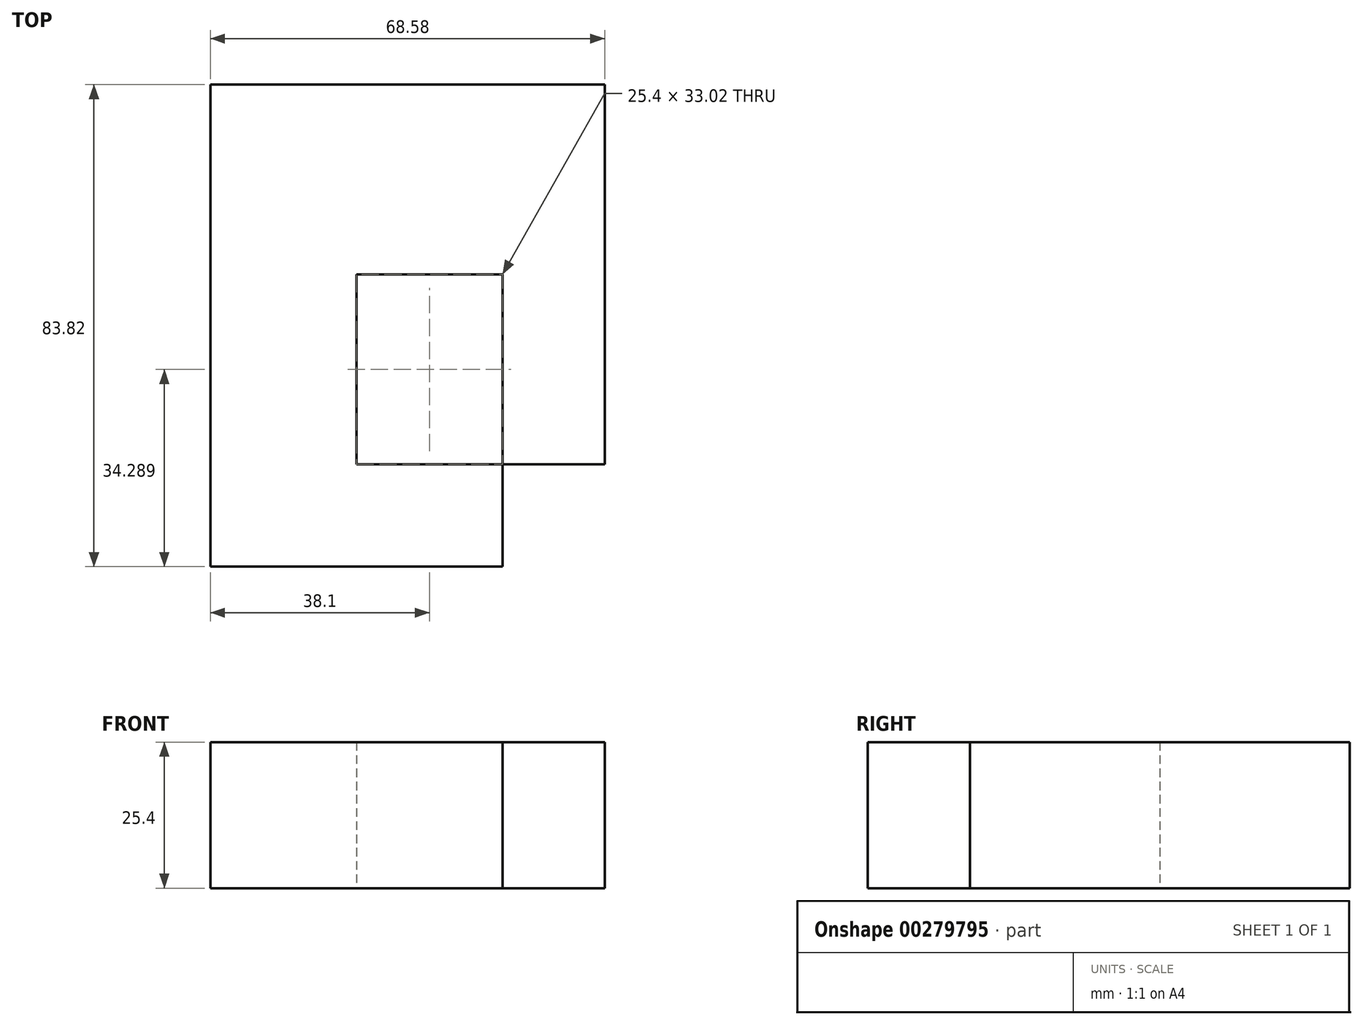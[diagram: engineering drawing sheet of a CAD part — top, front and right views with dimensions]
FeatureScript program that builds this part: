
annotation { "Feature Type Name" : "Feature", "Feature Type Description" : "" }
export const myFeature = defineFeature(function(context is Context, id is Id, definition is map)
    precondition{}
    {
        {
            var Q0;
            Q0=qCreatedBy(makeId("Right.planeOp"),FACE);
            var sketch = newSketch(context, id + "F0", { "sketchPlane" : qUnion([Q0])});
            skLineSegment(sketch, "E0.bottom", {"start": v(-62.3, -39.55) * mm, "end": v(3.74, -39.55) * mm});
            skLineSegment(sketch, "E0.top", {"start": v(-62.3, -64.95) * mm, "end": v(3.74, -64.95) * mm});
            skLineSegment(sketch, "E0.left", {"start": v(-62.3, -39.55) * mm, "end": v(-62.3, -64.95) * mm});
            skLineSegment(sketch, "E0.right", {"start": v(3.74, -39.55) * mm, "end": v(3.74, -64.95) * mm});
            skLineSegment(sketch, "E1", {"start": v(-29.28, -39.55) * mm, "end": v(-29.28, -64.95) * mm});
            skSolve(sketch);
        }
        {
            var Q0;
            {var subQ0=sQuery(id+"F0.wireOp",EDGE,"E0.left");Q0=makeQuery(id+"F0.imprint","IMPRINT",FACE,{"disambiguationData":[TD([[makeQuery(id+"F0.imprint","IMPRINT",EDGE,{"derivedFrom":subQ0}),1.0]])]});}
            extrude(context, id + "F1", {"entities" : qUnion([Q0]), "oppositeDirection" : true, "depth" : 17.78 * mm});
        }
        {
            var Q0;
            {var subQ0=sQuery(id+"F0.wireOp",EDGE,"E0.right");Q0=makeQuery(id+"F0.imprint","IMPRINT",FACE,{"disambiguationData":[TD([[makeQuery(id+"F0.imprint","IMPRINT",EDGE,{"derivedFrom":subQ0}),-1.0]])]});}
            extrude(context, id + "F2", {"entities" : qUnion([Q0]), "operationType" : NewBodyOperationType.ADD, "oppositeDirection" : true, "depth" : 68.58 * mm});
        }
        {
            var Q0;
            Q0=makeQuery(id+"F2.opExtrude","SWEPT_FACE",FACE,{"disambiguationData":[OSD([sQuery(id+"F0.wireOp",EDGE,"E1")])]});
            var sketch = newSketch(context, id + "F3", { "sketchPlane" : qUnion([Q0])});
            skLineSegment(sketch, "E2", {"start": v(-43.18, -39.55) * mm, "end": v(-43.18, -64.95) * mm});
            skSolve(sketch);
        }
        {
            var Q0;
            {var subQ0=sQuery(id+"F3.wireOp",EDGE,"E2");Q0=makeQuery(id+"F3.imprint","IMPRINT",FACE,{"disambiguationData":[TD([[makeQuery(id+"F3.imprint","IMPRINT",EDGE,{"derivedFrom":subQ0}),-1.0]])]});}
            extrude(context, id + "F4", {"entities" : qUnion([Q0]), "operationType" : NewBodyOperationType.ADD, "depth" : 50.8 * mm});
        }
        {
            var Q0;
            Q0=makeQuery(id+"F4.opExtrude","SWEPT_FACE",FACE,{"disambiguationData":[OSD([sQuery(id+"F3.wireOp",EDGE,"E2")])]});
            var sketch = newSketch(context, id + "F5", { "sketchPlane" : qUnion([Q0])});
            skLineSegment(sketch, "E3", {"start": v(-62.3, -39.55) * mm, "end": v(-62.3, -64.95) * mm});
            skSolve(sketch);
        }
        {
            var Q0;
            {var subQ0=sQuery(id+"F5.wireOp",EDGE,"E3");Q0=makeQuery(id+"F5.imprint","IMPRINT",FACE,{"disambiguationData":[TD([[makeQuery(id+"F5.imprint","IMPRINT",EDGE,{"derivedFrom":subQ0}),-1.0]])]});}
            extrude(context, id + "F6", {"entities" : qUnion([Q0]), "operationType" : NewBodyOperationType.ADD, "depth" : 25.43 * mm});
        }
    });
